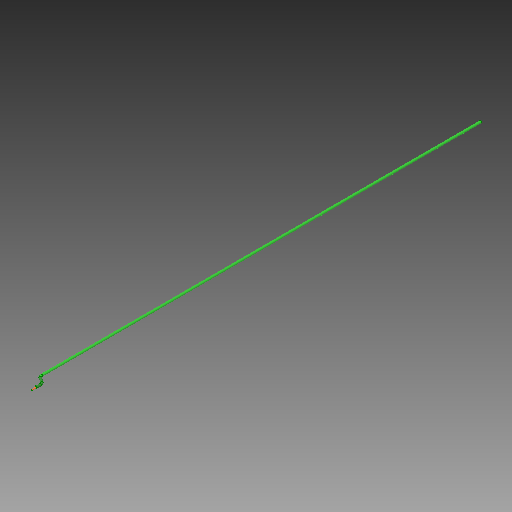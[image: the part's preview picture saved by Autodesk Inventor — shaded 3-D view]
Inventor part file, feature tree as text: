
AUTODESK INVENTOR PART (.ipt)
format: ipt  version: 2019 (Build 230136000, 136)  size: 81,920 bytes
history: native  units: in
note: dims shown in document units (in); Inventor stores cm internally (conversion verified against a paired STEP export)
features: sweep x1
ambient origin geometry x8: Origin, YZ Plane, XZ Plane, XY Plane, X Axis, Y Axis, Z Axis, Center Point
bodies: Solid1 (feature_tree)
feature tree (1):
  sweep  "Sweep1"
